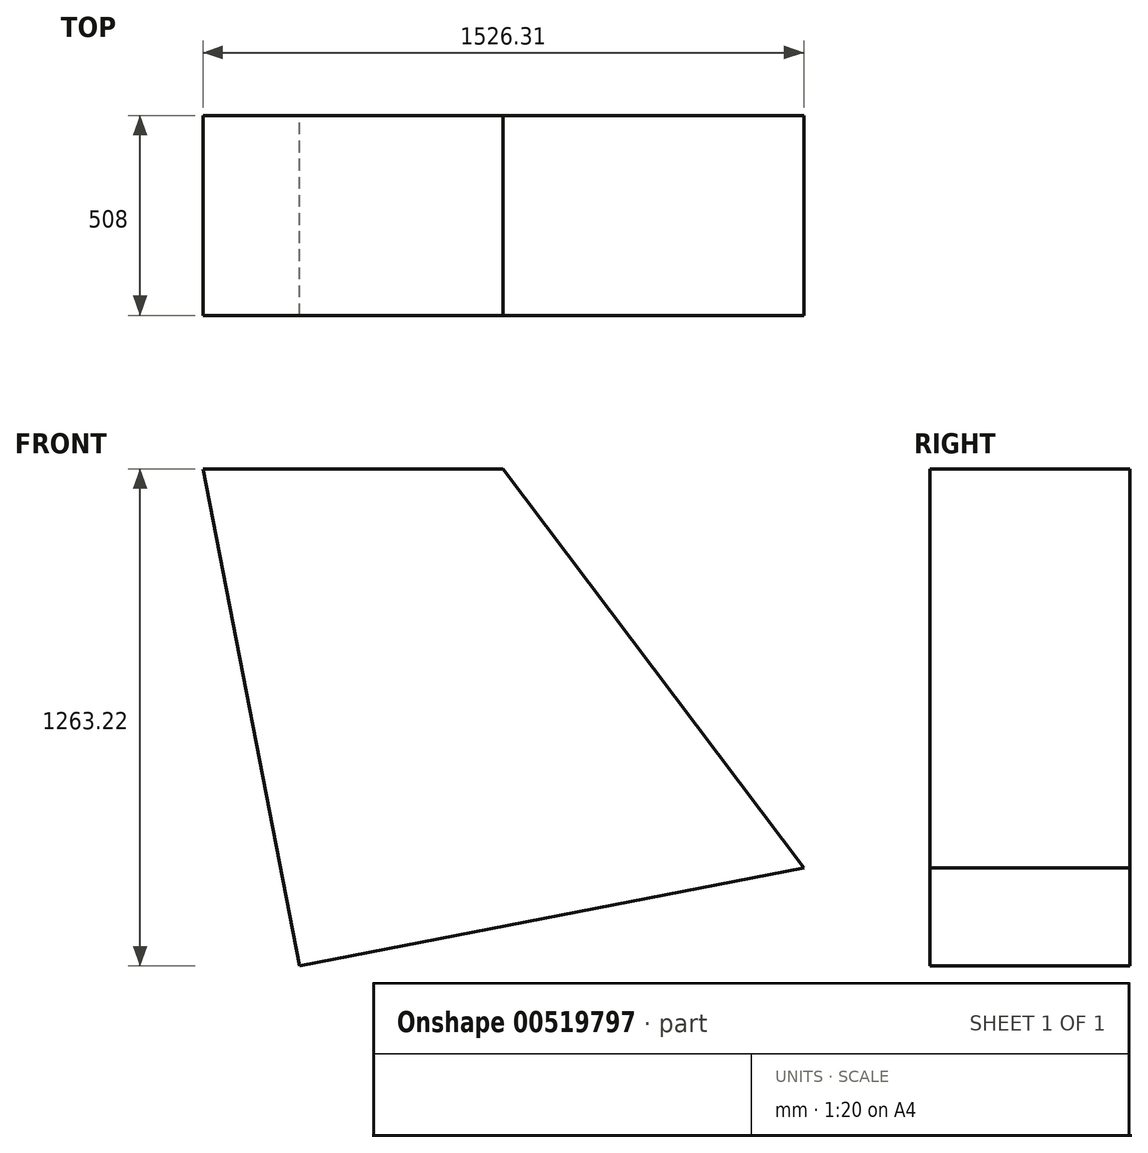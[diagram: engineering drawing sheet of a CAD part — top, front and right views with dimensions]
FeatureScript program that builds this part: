
annotation { "Feature Type Name" : "Feature", "Feature Type Description" : "" }
export const myFeature = defineFeature(function(context is Context, id is Id, definition is map)
    precondition{}
    {
        {
            var Q0;
            Q0=qCreatedBy(makeId("Front.planeOp"),FACE);
            var sketch = newSketch(context, id + "F0", { "sketchPlane" : qUnion([Q0])});
            skLineSegment(sketch, "E0", {"start": v(0, 0) * mm, "end": v(762, 0) * mm});
            skLineSegment(sketch, "E1", {"start": v(762, 0) * mm, "end": v(1526.3, -1014.27) * mm});
            skLineSegment(sketch, "E2", {"start": v(1526.3, -1014.27) * mm, "end": v(245.55, -1263.22) * mm});
            skLineSegment(sketch, "E3", {"start": v(0, 0) * mm, "end": v(245.55, -1263.22) * mm});
            skSolve(sketch);
        }
        {
            var Q0;
            Q0 = qSketchRegion(id + "F0", true);
            extrude(context, id + "F1", {"entities" : qUnion([Q0]), "depth" : 508 * mm, "offsetDistance" : 25.4 * mm});
        }
    });
